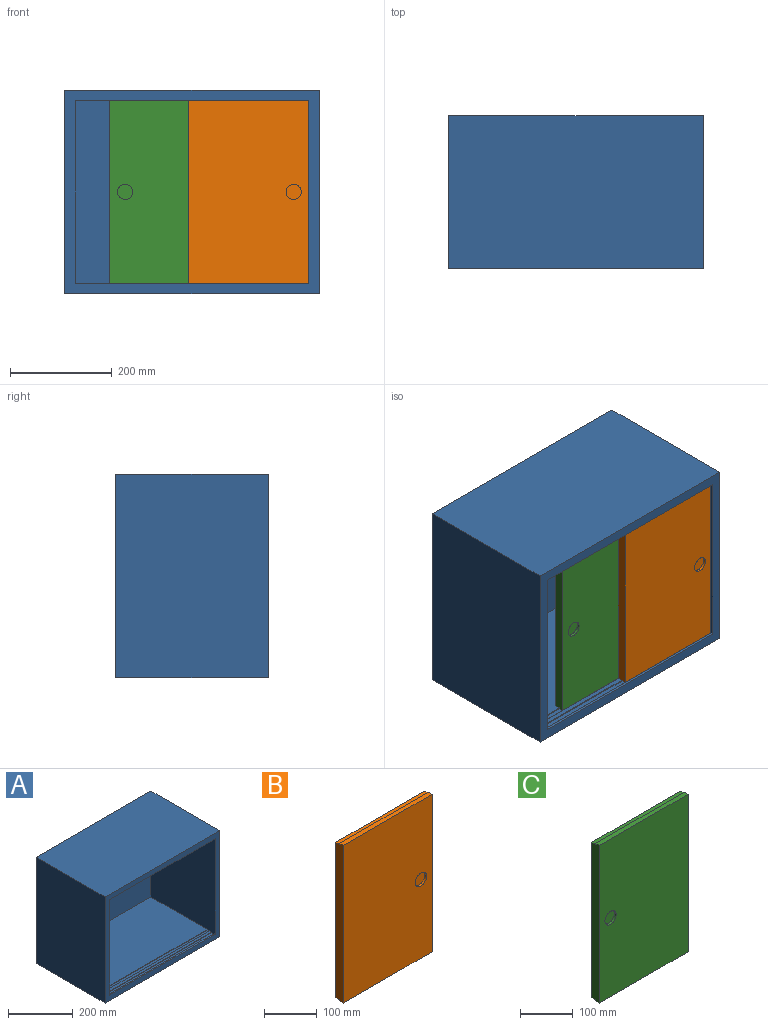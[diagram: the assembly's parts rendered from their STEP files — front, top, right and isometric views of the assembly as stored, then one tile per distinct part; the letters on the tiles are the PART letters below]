
ASSEMBLY  parts=3 mates=2
PART A: 27 faces, bbox 500x300x400 mm
  f0: plane 460x10mm, normal (0,0,-1), area 4600mm2, adj f10,f12,f21,f24
  f1: plane 460x245mm, normal (0,0,-1), area 112700mm2, adj f10,f11,f12,f22
  f2: plane 460x10mm, normal (0,0,1), area 4600mm2, adj f10,f12,f17,f19
  f3: plane 460x245mm, normal (0,0,1), area 112700mm2, adj f10,f11,f12,f16
  f4: plane 500x400mm, normal (0,-1,0), area 34400mm2, adj f5,f7,f8,f9,f10,f12,f13,f14
  f5: plane 400x300mm, normal (1,0,0), area 120000mm2, adj f4,f6,f8,f9
  f6: plane 500x400mm, normal (0,1,0), area 200000mm2, adj f5,f7,f8,f9
  f7: plane 400x300mm, normal (-1,0,0), area 120000mm2, adj f4,f6,f8,f9
  f8: plane 500x300mm, normal (0,0,1), area 150000mm2, adj f4,f5,f6,f7
  f9: plane 500x300mm, normal (0,0,-1), area 150000mm2, adj f4,f5,f6,f7
  f10: plane 367x280mm, normal (-1,0,0), area 100940mm2, adj f0,f1,f2,f3,f4,f11,f13,f14
  f11: plane 460x360mm, normal (0,-1,0), area 165600mm2, adj f1,f3,f10,f12
  f12: plane 367x280mm, normal (1,0,0), area 100940mm2, adj f0,f1,f2,f3,f4,f11,f13,f14
  f13: plane 460x5mm, normal (0,0,-1), area 2300mm2, adj f4,f10,f12,f25
  f14: plane 460x5mm, normal (0,0,1), area 2300mm2, adj f4,f10,f12,f20
  f15: plane 460x10mm, normal (0,0,1), area 4600mm2, adj f10,f12,f16,f17
  f16: plane 460x2mm, normal (0,-1,0), area 920mm2, adj f3,f10,f12,f15
  f17: plane 460x2mm, normal (0,1,0), area 920mm2, adj f2,f10,f12,f15
  f18: plane 460x10mm, normal (0,0,1), area 4600mm2, adj f10,f12,f19,f20
  f19: plane 460x2mm, normal (0,-1,0), area 920mm2, adj f2,f10,f12,f18
  f20: plane 460x2mm, normal (0,1,0), area 920mm2, adj f10,f12,f14,f18
  f21: plane 460x5mm, normal (0,1,0), area 2300mm2, adj f0,f10,f12,f23
  f22: plane 460x5mm, normal (0,-1,0), area 2300mm2, adj f1,f10,f12,f23
  f23: plane 460x10mm, normal (0,0,-1), area 4600mm2, adj f10,f12,f21,f22
  f24: plane 460x5mm, normal (0,-1,0), area 2300mm2, adj f0,f10,f12,f26
  f25: plane 460x5mm, normal (0,1,0), area 2300mm2, adj f10,f12,f13,f26
  f26: plane 460x10mm, normal (0,0,-1), area 4600mm2, adj f10,f12,f24,f25
PART B: 12 faces, bbox 237.5x20x364.5 mm
  f0: plane 360x237.5mm, normal (0,1,0), area 85500mm2, adj f3,f4,f7,f8
  f1: plane 364.5x237.5mm, normal (0,-1,0), area 85861.9mm2, adj f2,f3,f8,f9,f10
  f2: plane 237.5x10mm, normal (0,0,-1), area 2375mm2, adj f1,f3,f6,f8
  f3: plane 364.5x20mm, normal (1,0,0), area 7245mm2, adj f0,f1,f2,f4,f5,f6,f7,f9
  f4: plane 237.5x10mm, normal (0,0,1), area 2375mm2, adj f0,f3,f5,f8
  f5: plane 237.5x2.5mm, normal (0,1,0), area 593.8mm2, adj f3,f4,f8,f9
  f6: plane 237.5x2mm, normal (0,1,0), area 475mm2, adj f2,f3,f7,f8
  f7: plane 237.5x10mm, normal (0,0,-1), area 2375mm2, adj f0,f3,f6,f8
  f8: plane 364.5x20mm, normal (-1,0,0), area 7245mm2, adj f0,f1,f2,f4,f5,f6,f7,f9
  f9: plane 237.5x10mm, normal (0,0,1), area 2375mm2, adj f1,f3,f5,f8
  f10: cylinder r=15mm len=30mm, axis (0,-1,0), area 471.2mm2, adj f1,f11
  f11: plane 30x30mm, normal (0,-1,0), area 706.9mm2, adj f10
PART C: 12 faces, bbox 237.5x20x364.5 mm
  f0: plane 360x237.5mm, normal (0,1,0), area 85500mm2, adj f3,f4,f7,f8
  f1: plane 364.5x237.5mm, normal (0,-1,0), area 85861.9mm2, adj f2,f3,f8,f9,f10
  f2: plane 237.5x10mm, normal (0,0,-1), area 2375mm2, adj f1,f3,f6,f8
  f3: plane 364.5x20mm, normal (-1,0,0), area 7245mm2, adj f0,f1,f2,f4,f5,f6,f7,f9
  f4: plane 237.5x10mm, normal (0,0,1), area 2375mm2, adj f0,f3,f5,f8
  f5: plane 237.5x2.5mm, normal (0,1,0), area 593.8mm2, adj f3,f4,f8,f9
  f6: plane 237.5x2mm, normal (0,1,0), area 475mm2, adj f2,f3,f7,f8
  f7: plane 237.5x10mm, normal (0,0,-1), area 2375mm2, adj f0,f3,f6,f8
  f8: plane 364.5x20mm, normal (1,0,0), area 7245mm2, adj f0,f1,f2,f4,f5,f6,f7,f9
  f9: plane 237.5x10mm, normal (0,0,1), area 2375mm2, adj f1,f3,f5,f8
  f10: cylinder r=15mm len=30mm, axis (0,-1,0), area 471.2mm2, adj f1,f11
  f11: plane 30x30mm, normal (0,-1,0), area 706.9mm2, adj f10
PLACE A at identity fixed
PLACE B at identity
PLACE C t=(68.55,0,0)mm
MATE slider A.f10 <-> B.f3  axis (-1,0,0) through (230,-135,20)mm
MATE slider A.f12 <-> C.f3  axis (1,0,0) through (-230,-115,20)mm
